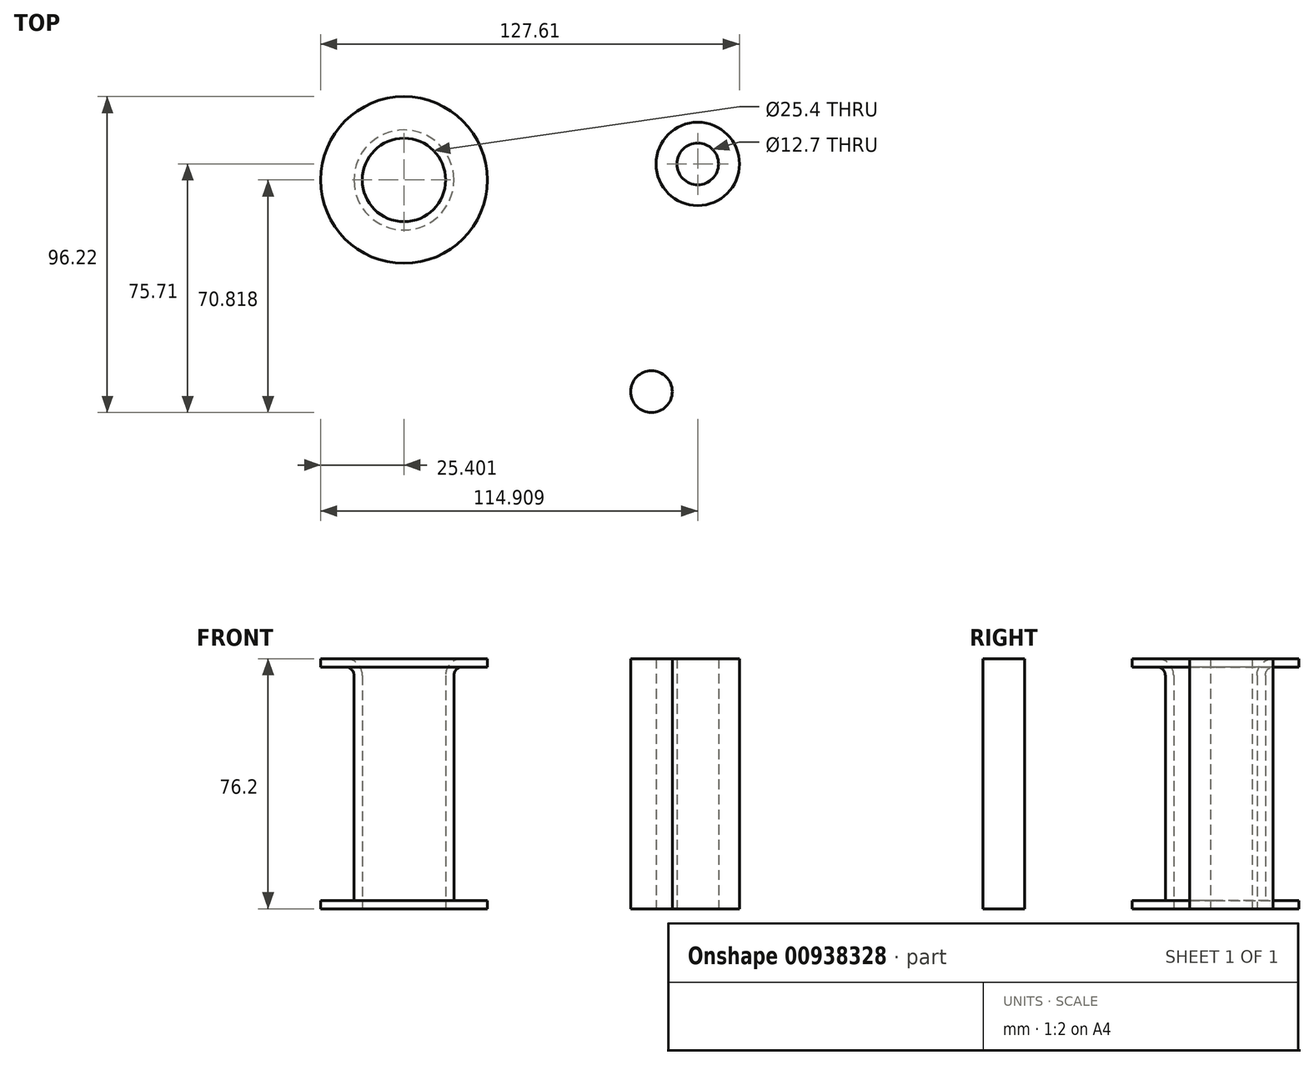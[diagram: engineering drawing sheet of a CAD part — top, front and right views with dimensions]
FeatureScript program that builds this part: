
annotation { "Feature Type Name" : "Feature", "Feature Type Description" : "" }
export const myFeature = defineFeature(function(context is Context, id is Id, definition is map)
    precondition{}
    {
        {
            var Q0;
            Q0=qCreatedBy(makeId("Top.planeOp"),FACE);
            var sketch = newSketch(context, id + "F0", { "sketchPlane" : qUnion([Q0])});
            skCircle(sketch, "E0", {"center": v(-51.95, 27.2) * mm, "radius": 25.4 * mm});
            skCircle(sketch, "E1", {"center": v(-51.95, 27.2) * mm, "radius": 12.7 * mm});
            skCircle(sketch, "E2", {"center": v(37.56, 32.1) * mm, "radius": 12.7 * mm});
            skCircle(sketch, "E3", {"center": v(37.56, 32.1) * mm, "radius": 6.35 * mm});
            skCircle(sketch, "E4", {"center": v(23.46, -37.27) * mm, "radius": 6.35 * mm});
            skSolve(sketch);
        }
        {
            var Q0;
            Q0=makeQuery(id+"F0.imprint","IMPRINT",FACE,{"disambiguationData":[TD([[makeQuery(id+"F0.imprint","IMPRINT",EDGE,{"derivedFrom":sQuery(id+"F0.wireOp",EDGE,"E0")}),1.0]])]});
            var Q1;
            Q1=makeQuery(id+"F0.imprint","IMPRINT",FACE,{"disambiguationData":[TD([[makeQuery(id+"F0.imprint","IMPRINT",EDGE,{"derivedFrom":sQuery(id+"F0.wireOp",EDGE,"E2")}),1.0]])]});
            var Q2;
            Q2=makeQuery(id+"F0.imprint","IMPRINT",FACE,{"disambiguationData":[TD([[makeQuery(id+"F0.imprint","IMPRINT",EDGE,{"derivedFrom":sQuery(id+"F0.wireOp",EDGE,"E4")}),1.0]])]});
            extrude(context, id + "F1", {"entities" : qUnion([Q0, Q1, Q2]), "depth" : 76.2 * mm, "offsetDistance" : 25.4 * mm});
        }
        {
            var Q0;
            Q0=makeQuery(id+"F1.opExtrude","CAP_EDGE",EDGE,{"disambiguationData":[OSD([sQuery(id+"F0.wireOp",EDGE,"E1")])],"isStart":false});
            fillet(context, id + "F2", {"entities" : qUnion([Q0]), "radius" : 5.08 * mm, "tangentPropagation" : true, "allowEdgeOverflow" : false});
        }
        {
            var Q0;
            Q0=makeQuery(id+"F1.opExtrude","SWEPT_FACE",FACE,{"disambiguationData":[OSD([sQuery(id+"F0.wireOp",EDGE,"E0")])]});
            shell(context, id + "F3", {"entities" : qUnion([Q0]), "thickness" : 2.54 * mm});
        }
    });
